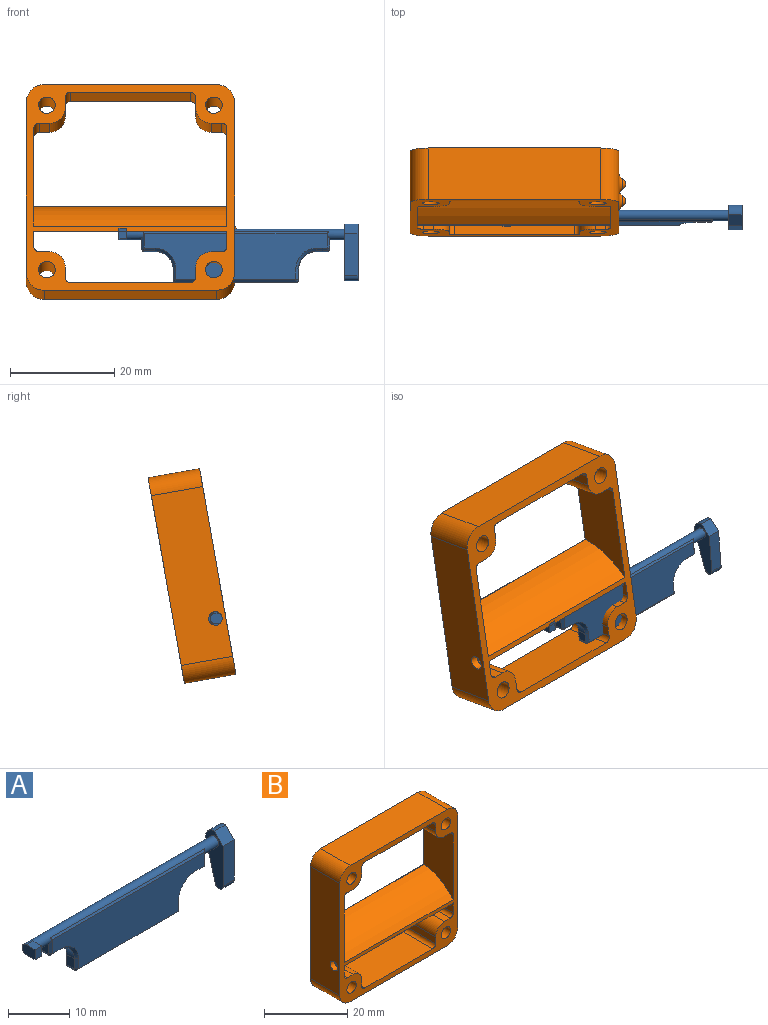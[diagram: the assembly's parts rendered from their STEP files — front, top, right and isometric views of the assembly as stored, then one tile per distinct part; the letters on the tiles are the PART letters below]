
ASSEMBLY  parts=2 mates=1
PART A: 43 faces, bbox 45.8x4x11.2 mm
  f0: plane 2.78x1.7mm, normal (-1,0,0), area 3.2mm2, adj f1,f2,f13,f29,f30
  f1: plane 36x8mm, normal (0,1,0), area 221.1mm2, adj f0,f3,f4,f5,f6,f7,f8,f9
  f2: cylinder r=1mm len=43.3mm, axis (-1,0,0), area 133.4mm2, adj f0,f15,f22,f23,f24,f25,f27,f28
  f3: cylinder r=0.5mm len=1.7mm, axis (0,1,0), area 1.3mm2, adj f1,f4,f15,f41
  f4: plane 2x1.7mm, normal (0,0,-1), area 3.4mm2, adj f1,f3,f5,f40
  f5: cylinder r=3.5mm len=3.5mm, axis (0,1,0), area 9.3mm2, adj f1,f4,f6,f39
  f6: plane 2x1.7mm, normal (1,0,0), area 3.4mm2, adj f1,f5,f7,f38
  f7: cylinder r=0.5mm len=1.7mm, axis (0,1,0), area 1.3mm2, adj f1,f6,f8,f37
  f8: plane 23x1.7mm, normal (0,0,-1), area 39.1mm2, adj f1,f7,f9,f36
  f9: cylinder r=0.5mm len=1.7mm, axis (0,1,0), area 1.3mm2, adj f1,f8,f10,f35
  f10: plane 2x1.7mm, normal (-1,0,0), area 3.4mm2, adj f1,f9,f11,f34
  f11: cylinder r=3.5mm len=3.5mm, axis (0,1,0), area 9.3mm2, adj f1,f10,f12,f33
  f12: plane 2x1.7mm, normal (0,0,-1), area 3.4mm2, adj f1,f11,f13,f32
  f13: cylinder r=0.5mm len=1.7mm, axis (0,1,0), area 1.3mm2, adj f0,f1,f12,f31
  f14: plane 35x8.79mm, normal (0,-1,0), area 242.7mm2, adj f28,f30,f32,f33,f34,f36,f38,f39
  f15: plane 2.78x1.7mm, normal (1,0,0), area 3.2mm2, adj f1,f2,f3,f29,f42
  f16: plane 2.5x2mm, normal (0,-0.71,0.71), area 7.1mm2, adj f17,f20,f21,f22
  f17: plane 8x2.5mm, normal (0,-1,0), area 20mm2, adj f16,f18,f21,f22
  f18: cylinder r=0.95mm len=2.5mm, axis (-1,0,0), area 6.8mm2, adj f17,f19,f21,f22
  f19: plane 7.73x2.5mm, normal (0,0.97,-0.26), area 20mm2, adj f18,f20,f21,f22
  f20: cylinder r=2mm len=2.52mm, axis (-1,0,0), area 9.2mm2, adj f16,f19,f21,f22
  f21: plane 10.95x4mm, normal (1,0,0), area 30.5mm2, adj f16,f17,f18,f19,f20
  f22: plane 10.95x4mm, normal (-1,0,0), area 27.4mm2, adj f2,f16,f17,f18,f19,f20
  f23: plane 2x2mm, normal (1,0,0), area 2.4mm2, adj f2,f24,f25,f26
  f24: plane 2x1.5mm, normal (0,0,1), area 3mm2, adj f2,f23,f26,f27
  f25: plane 2x1.5mm, normal (0,0,-1), area 3mm2, adj f2,f23,f26,f27
  f26: plane 2x1.5mm, normal (0,-1,0), area 3mm2, adj f23,f24,f25,f27
  f27: plane 3x2mm, normal (-1,0,0), area 5.6mm2, adj f2,f24,f25,f26
  f28: plane 35.47x0.41mm, normal (0,-0.87,0.5), area 16.5mm2, adj f2,f14,f30,f42
  f29: plane 36x1.28mm, normal (0,1,0.08), area 46.2mm2, adj f0,f1,f2,f15
  f30: plane 3.2x0.5mm, normal (-0.71,-0.71,0), area 1.6mm2, adj f0,f2,f14,f28,f31
  f31: cone r=0.5mm half-angle=45deg, axis (0,1,0), area 0.3mm2, adj f13,f30,f32
  f32: plane 2x0.5mm, normal (0,-0.71,-0.71), area 1.4mm2, adj f12,f14,f31,f33
  f33: cone r=4mm half-angle=45deg, axis (0,-1,0), area 4.2mm2, adj f11,f14,f32,f34
  f34: plane 2x0.5mm, normal (-0.71,-0.71,0), area 1.4mm2, adj f10,f14,f33,f35
  f35: cone r=0.5mm half-angle=45deg, axis (0,1,0), area 0.3mm2, adj f9,f34,f36
  f36: plane 23x0.5mm, normal (0,-0.71,-0.71), area 16.3mm2, adj f8,f14,f35,f37
  f37: cone r=0.5mm half-angle=45deg, axis (0,1,0), area 0.3mm2, adj f7,f36,f38
  f38: plane 2x0.5mm, normal (0.71,-0.71,0), area 1.4mm2, adj f6,f14,f37,f39
  f39: cone r=4mm half-angle=45deg, axis (0,-1,0), area 4.2mm2, adj f5,f14,f38,f40
  f40: plane 2x0.5mm, normal (0,-0.71,-0.71), area 1.4mm2, adj f4,f14,f39,f41
  f41: cone r=0.5mm half-angle=45deg, axis (0,1,0), area 0.3mm2, adj f3,f40,f42
  f42: plane 3.2x0.5mm, normal (0.71,-0.71,0), area 1.6mm2, adj f2,f14,f15,f28,f41
PART B: 52 faces, bbox 41.5x11.5x40 mm
  f0: plane 0.09x0.09mm, normal (1,0,0), area 0mm2, adj f1
  f1: torus R=0.04mm, axis (-1,0,0), area 3.6mm2, adj f0
  f2: plane 0.09x0.09mm, normal (1,0,0), area 0mm2, adj f3
  f3: torus R=0.04mm, axis (-1,0,0), area 3.6mm2, adj f2
  f4: plane 37x2mm, normal (0,0.54,-0.84), area 88.3mm2, adj f5,f49,f50,f51
  f5: cylinder r=30.19mm len=37mm, axis (-1,0,0), area 343.3mm2, adj f4,f6,f49,f51
  f6: plane 40.01x40mm, normal (0,1,0), area 341.1mm2, adj f5,f7,f8,f10,f11,f12,f13,f14
  f7: cylinder r=3.5mm len=10mm, axis (0,1,0), area 55mm2, adj f6,f8,f18,f50
  f8: plane 33x10mm, normal (-1,0,0), area 324.7mm2, adj f6,f7,f9,f10,f50
  f9: cylinder r=1.3mm len=2.6mm, axis (1,0,0), area 12.3mm2, adj f8,f49
  f10: cylinder r=3.5mm len=10mm, axis (0,-1,0), area 55mm2, adj f6,f8,f11,f50
  f11: plane 33x10mm, normal (0,0,-1), area 330mm2, adj f6,f10,f12,f50
  f12: cylinder r=3.5mm len=10mm, axis (0,1,0), area 55mm2, adj f6,f11,f14,f50
  f13: torus R=2.24mm, axis (1,0,0), area 15mm2, adj f6,f14
  f14: plane 33x10mm, normal (1,0,0), area 293.5mm2, adj f6,f12,f13,f15,f16,f17,f50
  f15: cylinder r=1.3mm len=2.6mm, axis (1,0,0), area 12.3mm2, adj f14,f51
  f16: torus R=2.24mm, axis (1,0,0), area 15.2mm2, adj f14
  f17: cylinder r=3.5mm len=10mm, axis (0,-1,0), area 55mm2, adj f6,f14,f18,f50
  f18: plane 33x10mm, normal (0,0,1), area 330mm2, adj f6,f7,f17,f50
  f19: cylinder r=1.6mm len=10mm, axis (0,1,0), area 100.5mm2, adj f6,f50
  f20: cylinder r=1.6mm len=10mm, axis (0,1,0), area 100.5mm2, adj f6,f50
  f21: cylinder r=1.6mm len=10mm, axis (0,1,0), area 100.5mm2, adj f6,f50
  f22: cylinder r=1.6mm len=10mm, axis (0,1,0), area 100.5mm2, adj f6,f50
  f23: plane 19x10mm, normal (1,0,0), area 154.5mm2, adj f6,f24,f25,f37,f50
  f24: cylinder r=16.18mm len=37mm, axis (-1,0,0), area 425.1mm2, adj f23,f36,f37,f50
  f25: cylinder r=1mm len=10mm, axis (0,-1,0), area 15.7mm2, adj f6,f23,f26,f50
  f26: plane 10x2mm, normal (0,0,-1), area 20mm2, adj f6,f25,f27,f50
  f27: cylinder r=3mm len=10mm, axis (0,-1,0), area 47.1mm2, adj f6,f26,f28,f50
  f28: plane 10x2mm, normal (1,0,0), area 20mm2, adj f6,f27,f29,f50
  f29: cylinder r=1mm len=10mm, axis (0,1,0), area 15.7mm2, adj f6,f28,f30,f50
  f30: plane 23x10mm, normal (0,0,-1), area 230mm2, adj f6,f29,f31,f50
  f31: cylinder r=1mm len=10mm, axis (0,-1,0), area 15.7mm2, adj f6,f30,f32,f50
  f32: plane 10x2mm, normal (-1,0,0), area 20mm2, adj f6,f31,f33,f50
  f33: cylinder r=3mm len=10mm, axis (0,-1,0), area 47.1mm2, adj f6,f32,f34,f50
  f34: plane 10x2mm, normal (0,0,-1), area 20mm2, adj f6,f33,f35,f50
  f35: cylinder r=1mm len=10mm, axis (0,1,0), area 15.7mm2, adj f6,f34,f36,f50
  f36: plane 19x10mm, normal (-1,0,0), area 154.5mm2, adj f6,f24,f35,f37,f50
  f37: cylinder r=0.15mm len=37mm, axis (-1,0,0), area 9.6mm2, adj f6,f23,f24,f36
  f38: cylinder r=1mm len=10mm, axis (0,-1,0), area 15.7mm2, adj f6,f39,f50,f51
  f39: plane 10x2mm, normal (0,0,1), area 20mm2, adj f6,f38,f40,f50
  f40: cylinder r=3mm len=10mm, axis (0,-1,0), area 47.1mm2, adj f6,f39,f41,f50
  f41: plane 10x2mm, normal (-1,0,0), area 20mm2, adj f6,f40,f42,f50
  f42: cylinder r=1mm len=10mm, axis (0,1,0), area 15.7mm2, adj f6,f41,f43,f50
  f43: plane 23x10mm, normal (0,0,1), area 230mm2, adj f6,f42,f44,f50
  f44: cylinder r=1mm len=10mm, axis (0,-1,0), area 15.7mm2, adj f6,f43,f45,f50
  f45: plane 10x2mm, normal (1,0,0), area 20mm2, adj f6,f44,f46,f50
  f46: cylinder r=3mm len=10mm, axis (0,-1,0), area 47.1mm2, adj f6,f45,f47,f50
  f47: plane 10x2mm, normal (0,0,1), area 20mm2, adj f6,f46,f48,f50
  f48: cylinder r=1mm len=10mm, axis (0,1,0), area 15.7mm2, adj f6,f47,f49,f50
  f49: plane 10.01x8.94mm, normal (1,0,0), area 57.1mm2, adj f4,f5,f6,f9,f48,f50
  f50: plane 40x40mm, normal (0,-1,0), area 363.3mm2, adj f4,f7,f8,f10,f11,f12,f14,f17
  f51: plane 10.01x8.94mm, normal (-1,0,0), area 57.1mm2, adj f4,f5,f6,f15,f38,f50
PLACE A rot(axis=(-1,0,0),5deg) t=(-94.34,-32.37,-13.51)mm
PLACE B rot(axis=(-1,0,0),10deg) t=(-114.54,-31.7,-14.31)mm
MATE revolute A.f2 <-> B.f9  axis (-1,0,0) through (-95.09,-41.11,-21.58)mm
